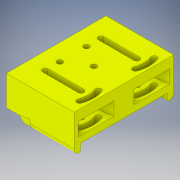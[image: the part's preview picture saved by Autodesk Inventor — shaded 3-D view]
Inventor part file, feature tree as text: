
AUTODESK INVENTOR PART (.ipt)
format: ipt  version: 2019 (Build 230136000, 136)  size: 568,320 bytes
history: native  units: in
note: dims shown in document units (in); Inventor stores cm internally (conversion verified against a paired STEP export)
features: extrude x20, sketch x18, fillet x2, loft x1, mirror x1, hole x1, other x1
ambient origin geometry x8: Origin, YZ Plane, XZ Plane, XY Plane, X Axis, Y Axis, Z Axis, Center Point
bodies: Solid1 (feature_tree)
feature tree (44):
  sketch  "Sketch1"  dims[d0=0.5497in d1=0.3937in]
  sketch  "Sketch2"  dims[d2=0.3937in d3=0.3937in]
  extrude  "Extrusion1"  Depth=0.3937in
  extrude  "Extrusion2"  Depth=0.3937in
  sketch  "Sketch3"  dims[d4=3.937in d5=0.7874in]
  extrude  "Extrusion3"  Depth=0.7874in
  extrude  "Extrusion5"  Depth=0.3937in
  extrude  "Extrusion6"  Depth=1.1811in
  extrude  "Extrusion7"  Depth=0.3937in TaperAngle=0.0deg
  extrude  "Extrusion9"  Depth=1.1811in TaperAngle=0.0deg
  loft  "Loft1"
  mirror  "Mirror2"
  extrude  "Extrusion10"  Depth=0.5236in
  sketch  "Sketch12"  dims[d28=0.1181in d29=1.9685in d30=0.0in]
  sketch  "Sketch13"  dims[d31=0.2205in d35=0.9843in]
  extrude  "Extrusion13"  Depth=1.9685in TaperAngle=0.0deg
  sketch  "Sketch14"  dims[d36=0.1374in d37=0.2749in]
  hole  "Hole3"  [1 undecoded]
  extrude  "Extrusion16"  Depth=0.2749in
  extrude  "Extrusion12"  Depth=0.1374in
  extrude  "Extrusion26"  Depth=1.2992in
  extrude  "Extrusion27"  Depth=0.3622in
  extrude  "Extrusion14"  Depth=0.315in
  extrude  "Extrusion15"  Depth=0.315in
  extrude  "Extrusion17"  Depth=0.3937in
  extrude  "Extrusion28"  Depth=0.3937in
  extrude  "Extrusion11"  Depth=0.3937in
  extrude  "Extrusion29"  Depth=0.3937in TaperAngle=0.0deg
  fillet  "Fillet1"  Radius=0.3425in
  fillet  "Fillet2"  Radius=0.3425in
  extrude  "Extrusion30"  Depth=0.3937in
  sketch  "Sketch5"  dims[d6=0.3937in d7=2.7559in]
  sketch  "Sketch6"  dims[d8=75.0deg d9=1.1811in]
  sketch  "Sketch8"  dims[d10=0.3937in d13=3.937in d14=0.0in]
  sketch  "Sketch9"  dims[d15=1.1811in d16=0.0in d17=1.1811in d18=2.3622in d19=0.0in d20=0.0in]
  other  "Edges1"
  sketch  "Sketch10"  dims[d23=1.1811in d24=0.3937in d25=0.0in]
  sketch  "Sketch11"  dims[d26=0.7874in d27=0.5236in]
  sketch  "Sketch15"  dims[d38=1.2047in d39=0.1374in]
  sketch  "Sketch26"  dims[d40=0.2749in d41=1.2992in]
  sketch  "Sketch27"  dims[d42=1.5748in d43=0.0in d49=0.3622in]
  sketch  "Sketch28"  dims[d50=1.5748in d51=0.0in d53=0.315in]
  sketch  "Sketch29"  dims[d54=0.0in d55=90.0deg d56=0.0in d57=90.0deg d58=0.315in]
  sketch  "Sketch30"  dims[d59=0.3937in d60=0.0in d61=2.478in d62=0.3425in d63=0.3425in d64=0.1181in d65=0.0in d66=0.3425in d67=0.3425in d68=0.3543in d69=0.2362in d70=0.0in d85=0.2205in d86=1.1811in d87=0.0in d90=0.2362in d91=0.0in d92=0.2205in d93=0.2362in d94=0.1575in d95=0.0787in d96=90.0deg d97=0.1969in d98=0.8108in d99=0.0787in d100=0.2362in d101=0.0in d102=0.2205in d103=0.2205in d104=3.937in d105=0.3937in d106=0.0in d107=0.0in d108=1.1811in d109=3.937in d110=0.0in d111=0.7087in d112=0.1181in d113=0.0in d148=0.3937in d149=3.937in d150=2.3622in d151=1.378in d152=0.0in d153=1.378in d154=0.0in d155=1.5748in d156=1.5748in d157=0.7874in d158=0.0in d159=0.2362in d160=0.2362in d161=0.315in d162=0.0in d163=0.2362in d164=0.0787in d165=0.1575in d166=0.315in d167=0.0in d168=0.3425in]
note: 1 required parameter value undecoded (feature->parameter linkage not recoverable at this tier; creation-order binding heuristic only, values carry confidence <= 0.55)
